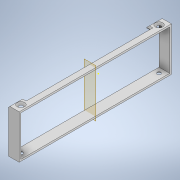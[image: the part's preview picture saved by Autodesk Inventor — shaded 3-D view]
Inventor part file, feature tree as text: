
AUTODESK INVENTOR PART (.ipt)
format: ipt  version: 2020.1 (Build 241239000, 239)  size: 147,968 bytes
history: native  units: mm
features: sketch x5, extrude x2, hole x2, plane x1, mirror x1, chamfer x1
ambient origin geometry x8: Origin, YZ Plane, XZ Plane, XY Plane, X Axis, Y Axis, Z Axis, Center Point
bodies: Solid1 (feature_tree)
feature tree (12):
  extrude  "Extrusion1"  Depth=45.4mm
  hole  "Hole1"  [1 undecoded]
  plane  "Work Plane1"
  mirror  "Mirror1"
  extrude  "Extrusion2"  Depth=8.0mm
  chamfer  "Chamfer1"  Distance=4.0mm
  sketch  "Sketch4"  dims[d7=4.0mm d8=6.0mm d9=8.4mm d10=2.0mm d11=90.0deg d12=10.0mm d13=20.594885mm]
  hole  "Hole2"  [1 undecoded]
  sketch  "Sketch1"  dims[d0=168.0mm d1=45.4mm]
  sketch  "Sketch2"  dims[d2=2.0mm d3=12.0mm d4=0.0mm]
  sketch  "Sketch3"  dims[d5=6.0mm d6=8.0mm]
  sketch  "Sketch5"  dims[d15=16.0mm d16=4.0mm d17=10.0mm d18=0.0mm d19=1.5mm d20=2.0mm d21=45.0deg d22=8.0mm d23=8.0mm d24=4.0mm d25=6.0mm d26=8.4mm d27=2.0mm d28=90.0deg d29=10.0mm d30=20.594885mm]
note: 2 required parameter values undecoded (feature->parameter linkage not recoverable at this tier; creation-order binding heuristic only, values carry confidence <= 0.55)
